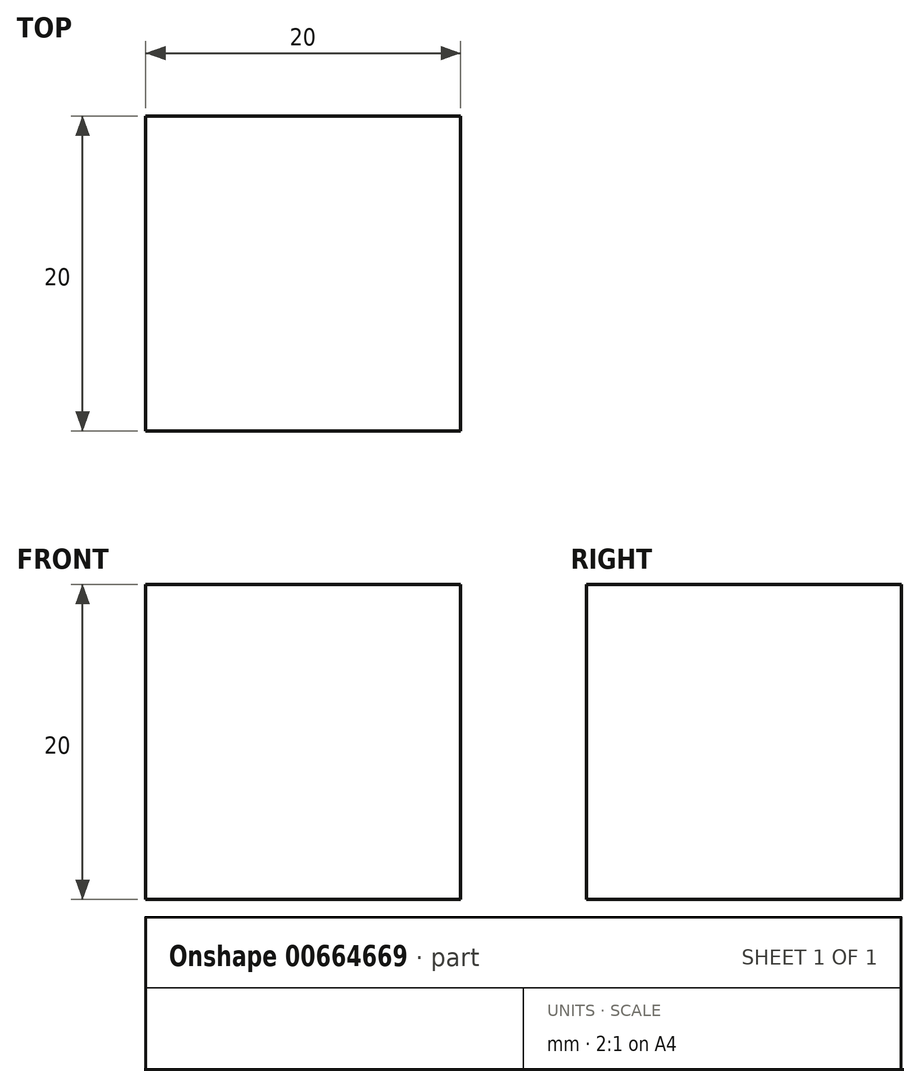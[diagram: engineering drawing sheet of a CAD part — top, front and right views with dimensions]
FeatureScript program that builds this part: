
annotation { "Feature Type Name" : "Feature", "Feature Type Description" : "" }
export const myFeature = defineFeature(function(context is Context, id is Id, definition is map)
    precondition{}
    {
        {
            var Q0;
            Q0=qCreatedBy(makeId("Top.planeOp"),FACE);
            var sketch = newSketch(context, id + "F0", { "sketchPlane" : qUnion([Q0])});
            skLineSegment(sketch, "E0.bottom", {"start": v(-114.65, 6.7) * mm, "end": v(-94.65, 6.7) * mm});
            skLineSegment(sketch, "E0.top", {"start": v(-114.65, -13.3) * mm, "end": v(-94.65, -13.3) * mm});
            skLineSegment(sketch, "E0.left", {"start": v(-114.65, 6.7) * mm, "end": v(-114.65, -13.3) * mm});
            skLineSegment(sketch, "E0.right", {"start": v(-94.65, 6.7) * mm, "end": v(-94.65, -13.3) * mm});
            skSolve(sketch);
        }
        {
            var Q0;
            Q0=makeQuery(id+"F0.imprint","IMPRINT",FACE,{"disambiguationData":[TD([[makeQuery(id+"F0.imprint","IMPRINT",EDGE,{"derivedFrom":sQuery(id+"F0.wireOp",EDGE,"E0.bottom")}),-1.0]])]});
            extrude(context, id + "F1", {"entities" : qUnion([Q0]), "depth" : 20 * mm, "offsetDistance" : 25.4 * mm});
        }
    });
